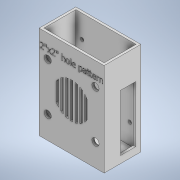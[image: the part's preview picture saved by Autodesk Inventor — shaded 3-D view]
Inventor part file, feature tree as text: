
AUTODESK INVENTOR PART (.ipt)
format: ipt  version: 2022.1 (Build 261234020, 234B)  size: 548,352 bytes
history: native  units: in
note: dims shown in document units (in); Inventor stores cm internally (conversion verified against a paired STEP export)
features: sketch x9, extrude x7, hole x2, mirror x1
ambient origin geometry x8: Origin, YZ Plane, XZ Plane, XY Plane, X Axis, Y Axis, Z Axis, Center Point
bodies: Solid2 (feature_tree)
feature tree (19):
  extrude  "Extrusion9"  Depth=3.9008in
  extrude  "Extrusion10"  TaperAngle=0.0deg  [1 undecoded]
  extrude  "Extrusion11"  Depth=3.7008in
  extrude  "Extrusion12"  TaperAngle=0.0deg  [1 undecoded]
  extrude  "Extrusion13"  TaperAngle=0.0deg  [1 undecoded]
  hole  "Hole3"  [1 undecoded]
  hole  "Hole4"  [1 undecoded]
  extrude  "Extrusion14"  Depth=2.5591in
  extrude  "Extrusion15"  TaperAngle=0.0deg  [1 undecoded]
  mirror  "Mirror2"
  sketch  "Sketch14"  dims[d66=2.7197in d67=3.9008in]
  sketch  "Sketch15"  dims[d68=0.1in d69=0.0in]
  sketch  "Sketch16"  dims[d70=2.5197in d71=3.7008in]
  sketch  "Sketch17"  dims[d72=1.3386in d73=0.0in]
  sketch  "Sketch18"  dims[d74=0.1in d75=0.0in]
  sketch  "Sketch19"  dims[d76=0.1in d77=0.0in]
  sketch  "Sketch22"  dims[d78=0.1969in d79=0.1181in]
  sketch  "Sketch23"  dims[d80=0.5906in d81=2.5591in]
  sketch  "Sketch24"  dims[d82=0.1in d83=0.0in d84=2.0in d85=2.0in d86=0.15in d87=0.276in d88=0.375in d89=0.25in d90=0.5635in d91=0.432in d92=0.0in d93=0.3in d94=0.75in d95=0.375in d96=0.25in d97=0.5635in d98=1.0in d99=0.0in d100=0.05in d101=0.0in d102=1.5in d104=0.1in d105=0.1in d106=0.1in d107=0.1in d108=0.1in d109=0.1in d110=1.0in d111=0.0in d103=0.75in]
note: 6 required parameter values undecoded (feature->parameter linkage not recoverable at this tier; creation-order binding heuristic only, values carry confidence <= 0.55)
